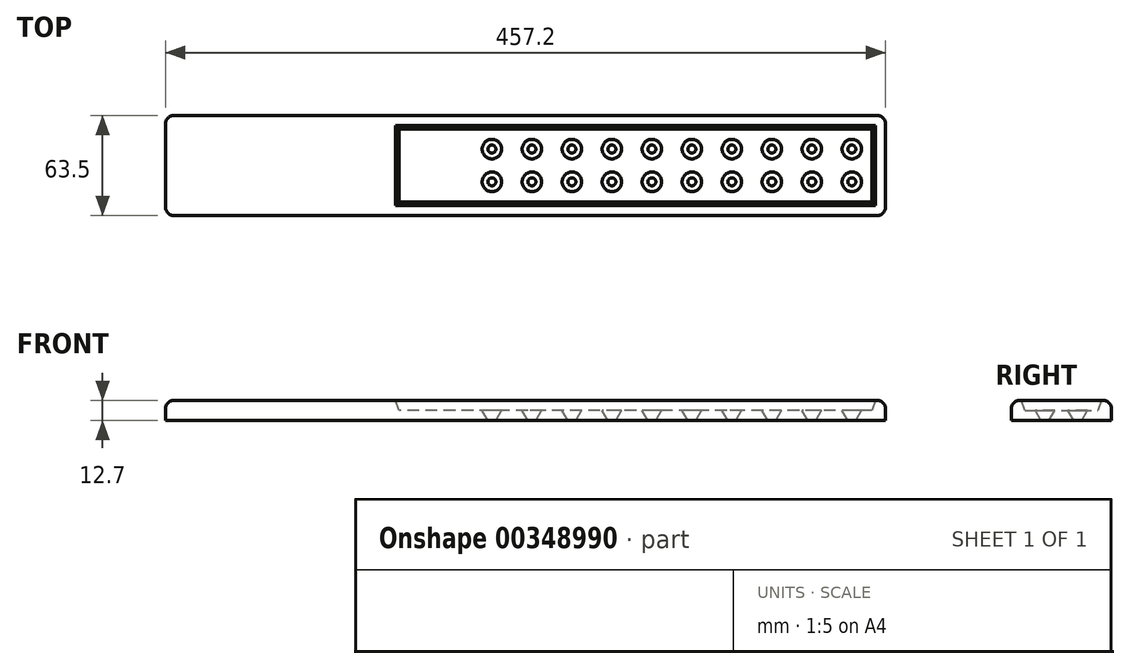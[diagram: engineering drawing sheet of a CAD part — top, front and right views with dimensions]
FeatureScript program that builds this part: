
annotation { "Feature Type Name" : "Feature", "Feature Type Description" : "" }
export const myFeature = defineFeature(function(context is Context, id is Id, definition is map)
    precondition{}
    {
        {
            var Q0;
            Q0=qCreatedBy(makeId("Top.planeOp"),FACE);
            var sketch = newSketch(context, id + "F0", { "sketchPlane" : qUnion([Q0])});
            skLineSegment(sketch, "E0.bottom", {"start": v(228.6, -31.75) * mm, "end": v(-228.6, -31.75) * mm});
            skLineSegment(sketch, "E0.top", {"start": v(228.6, 31.75) * mm, "end": v(-228.6, 31.75) * mm});
            skLineSegment(sketch, "E0.left", {"start": v(228.6, -31.75) * mm, "end": v(228.6, 31.75) * mm});
            skLineSegment(sketch, "E0.right", {"start": v(-228.6, -31.75) * mm, "end": v(-228.6, 31.75) * mm});
            skSolve(sketch);
        }
        {
            var Q0;
            Q0 = qSketchRegion(id + "F0", true);
            extrude(context, id + "F1", {"entities" : qUnion([Q0]), "oppositeDirection" : true, "depth" : 12.7 * mm});
        }
        {
            var Q0;
            Q0=makeQuery(id+"F1.opExtrude","CAP_FACE",FACE,{"disambiguationData":[OSD([sQuery(id+"F0.wireOp",EDGE,"E0.bottom"),sQuery(id+"F0.wireOp",EDGE,"E0.top"),sQuery(id+"F0.wireOp",EDGE,"E0.left"),sQuery(id+"F0.wireOp",EDGE,"E0.right")])],"isStart":true});
            var sketch = newSketch(context, id + "F2", { "sketchPlane" : qUnion([Q0])});
            skLineSegment(sketch, "E1.bottom", {"start": v(222.25, 25.4) * mm, "end": v(-82.55, 25.4) * mm});
            skLineSegment(sketch, "E1.top", {"start": v(222.25, -25.4) * mm, "end": v(-82.55, -25.4) * mm});
            skLineSegment(sketch, "E1.left", {"start": v(222.25, 25.4) * mm, "end": v(222.25, -25.4) * mm});
            skLineSegment(sketch, "E1.right", {"start": v(-82.55, 25.4) * mm, "end": v(-82.55, -25.4) * mm});
            skSolve(sketch);
        }
        {
            var Q0;
            Q0 = qSketchRegion(id + "F2", true);
            extrude(context, id + "F3", {"entities" : qUnion([Q0]), "operationType" : NewBodyOperationType.REMOVE, "oppositeDirection" : true, "depth" : 6.35 * mm, "hasDraft" : true, "draftAngle" : 20 * degree, "draftPullDirection" : true});
        }
        {
            var Q0;
            Q0=makeQuery(id+"F1.opExtrude","CAP_EDGE",EDGE,{"disambiguationData":[OSD([sQuery(id+"F0.wireOp",EDGE,"E0.top")])],"isStart":true});
            var Q1;
            Q1=makeQuery(id+"F1.opExtrude","CAP_EDGE",EDGE,{"disambiguationData":[OSD([sQuery(id+"F0.wireOp",EDGE,"E0.left")])],"isStart":true});
            var Q2;
            Q2=makeQuery(id+"F1.opExtrude","SWEPT_EDGE",EDGE,{"disambiguationData":[OSD([sQuery(id+"F0.wireOp",EDGE,"E0.top"),sQuery(id+"F0.wireOp",EDGE,"E0.left")])]});
            var Q3;
            Q3=makeQuery(id+"F1.opExtrude","SWEPT_EDGE",EDGE,{"disambiguationData":[OSD([sQuery(id+"F0.wireOp",EDGE,"E0.bottom"),sQuery(id+"F0.wireOp",EDGE,"E0.left")])]});
            var Q4;
            Q4=makeQuery(id+"F1.opExtrude","SWEPT_EDGE",EDGE,{"disambiguationData":[OSD([sQuery(id+"F0.wireOp",EDGE,"E0.top"),sQuery(id+"F0.wireOp",EDGE,"E0.right")])]});
            var Q5;
            Q5=makeQuery(id+"F1.opExtrude","CAP_EDGE",EDGE,{"disambiguationData":[OSD([sQuery(id+"F0.wireOp",EDGE,"E0.right")])],"isStart":true});
            var Q6;
            Q6=makeQuery(id+"F1.opExtrude","CAP_EDGE",EDGE,{"disambiguationData":[OSD([sQuery(id+"F0.wireOp",EDGE,"E0.bottom")])],"isStart":true});
            var Q7;
            Q7=makeQuery(id+"F1.opExtrude","SWEPT_EDGE",EDGE,{"disambiguationData":[OSD([sQuery(id+"F0.wireOp",EDGE,"E0.bottom"),sQuery(id+"F0.wireOp",EDGE,"E0.right")])]});
            fillet(context, id + "F4", {"entities" : qUnion([Q0, Q1, Q2, Q3, Q4, Q5, Q6, Q7]), "radius" : 5.08 * mm, "tangentPropagation" : true, "allowEdgeOverflow" : false});
        }
        {
            var Q0;
            Q0=makeQuery(id+"F1.opExtrude","CAP_FACE",FACE,{"disambiguationData":[OSD([sQuery(id+"F0.wireOp",EDGE,"E0.bottom"),sQuery(id+"F0.wireOp",EDGE,"E0.top"),sQuery(id+"F0.wireOp",EDGE,"E0.left"),sQuery(id+"F0.wireOp",EDGE,"E0.right")])],"isStart":false});
            var sketch = newSketch(context, id + "F5", { "sketchPlane" : qUnion([Q0])});
            skCircle(sketch, "E2", {"center": v(207.24, -10.39) * mm, "radius": 2.54 * mm});
            skCircle(sketch, "E3", {"center": v(207.24, 10.39) * mm, "radius": 2.54 * mm});
            skCircle(sketch, "E4.1.0.0", {"center": v(181.84, -10.39) * mm, "radius": 2.54 * mm});
            skCircle(sketch, "E4.1.0.1", {"center": v(181.84, 10.39) * mm, "radius": 2.54 * mm});
            skCircle(sketch, "E4.2.0.0", {"center": v(156.44, -10.39) * mm, "radius": 2.54 * mm});
            skCircle(sketch, "E4.2.0.1", {"center": v(156.44, 10.39) * mm, "radius": 2.54 * mm});
            skCircle(sketch, "E4.3.0.0", {"center": v(131.04, -10.39) * mm, "radius": 2.54 * mm});
            skCircle(sketch, "E4.3.0.1", {"center": v(131.04, 10.39) * mm, "radius": 2.54 * mm});
            skCircle(sketch, "E4.4.0.0", {"center": v(105.64, -10.39) * mm, "radius": 2.54 * mm});
            skCircle(sketch, "E4.4.0.1", {"center": v(105.64, 10.39) * mm, "radius": 2.54 * mm});
            skCircle(sketch, "E4.5.0.0", {"center": v(80.24, -10.39) * mm, "radius": 2.54 * mm});
            skCircle(sketch, "E4.5.0.1", {"center": v(80.24, 10.39) * mm, "radius": 2.54 * mm});
            skCircle(sketch, "E4.6.0.0", {"center": v(54.84, -10.39) * mm, "radius": 2.54 * mm});
            skCircle(sketch, "E4.6.0.1", {"center": v(54.84, 10.39) * mm, "radius": 2.54 * mm});
            skCircle(sketch, "E4.7.0.0", {"center": v(29.44, -10.39) * mm, "radius": 2.54 * mm});
            skCircle(sketch, "E4.7.0.1", {"center": v(29.44, 10.39) * mm, "radius": 2.54 * mm});
            skCircle(sketch, "E4.8.0.0", {"center": v(4.04, -10.39) * mm, "radius": 2.54 * mm});
            skCircle(sketch, "E4.8.0.1", {"center": v(4.04, 10.39) * mm, "radius": 2.54 * mm});
            skCircle(sketch, "E4.9.0.0", {"center": v(-21.36, -10.39) * mm, "radius": 2.54 * mm});
            skCircle(sketch, "E4.9.0.1", {"center": v(-21.36, 10.39) * mm, "radius": 2.54 * mm});
            skLineSegment(sketch, "E4.direction1", {"start": v(207.24, -10.39) * mm, "end": v(181.84, -10.39) * mm, "construction": true});
            skSolve(sketch);
        }
        {
            var Q0;
            Q0 = qSketchRegion(id + "F5", true);
            extrude(context, id + "F6", {"entities" : qUnion([Q0]), "operationType" : NewBodyOperationType.REMOVE, "endBound" : BoundingType.THROUGH_ALL, "oppositeDirection" : true, "depth" : 25.4 * mm, "hasDraft" : true, "draftAngle" : 30 * degree});
        }
    });
